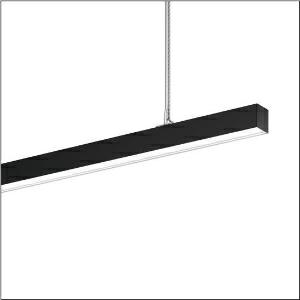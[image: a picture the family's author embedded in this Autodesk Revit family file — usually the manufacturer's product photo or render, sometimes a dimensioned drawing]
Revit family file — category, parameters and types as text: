
# Revit family: silica_r__21_51mx30db35bb_2e66
name_source: partatom
category: Lighting Fixtures
units: mm (PartAtom-declared; Revit-internal decimal feet)

## family parameters
Cut with Voids When Loaded = No
Host = Face
Light Source = No
Part Type = Normal
Room Calculation Point = No
Round Connector Dimension = Use Diameter
Shared = No

## types (1)
- --- (1 x LED, 5260 lm, 34.1 W, 3000K)
    Apparent Load = 34 VA
    CIE Flux Codes = 47 79 96 57 100
    Color Rendering = 80
    Color Temperature = 3000K
    Default Elevation = 1800 mm
    Description = Silica® 21, office luminaire, primary optical cover: cover, of PMMA, opal, light emission: direct/indirect distribution, primary light characteristic: symmetric, installation type: suspended mounting, LED, rated luminous flux: 5.260lm, luminous efficacy: 154lm/W, light colour: 830, colour temperature: 3000K, with terminal, 3+2-pole, max. 2.5mm², mains connection: 220..240V, AC, 50/60Hz, rated input power: 34.1W, luminaire housing, of aluminium, jet black (RAL 9005), length: 1.504mm, width: 53mm, height: 53mm, protection rating (complete): IP20, insulation class (complete): insulation class I (protective earthing), certification: CE, permissible operating ambient temperature: 0..+35°C, standard: EN 50419, packaging unit: 1 piece
    Height = 53 mm
    Lamp = 1 x LED
    Lamp Light Flux = 5260 lm
    Lamp Power = 34.1 W
    Lamp count = 1
    Length = 1504 mm
    Luminous efficacy = 154 lm/W
    Manufacturer = Siteco
    ModVariant = No
    Model = 51MX30DB35BB
    Mounting Place = Ceiling
    Mounting Type = Pendant
    Number of Poles = 1
    OnlyDefault = Yes
    Power Factor = 1
    Product Name = Silica® 21
    Product group = office luminaire | ceiling pendant
    ProductGroupID = 902
    Protection Class = Protection class I
    Protection Degree = IP 20
    RLX_Detail_Level = 1
    RLX_Emergency_Light_Flux = 0 lm
    RLX_Emergency_Type = 0
    RLX_Emergency_Type_DB = No
    RlxData = <blob elided: 26009 chars, md5=28c731c8>
    Socket = socket
    Standby Power = 0 W
    System Light Flux = 5260 lm
    System Power = 34 W
    Type Comments = factory setting: luminous flux: 100 % | dim-lin: 254 | 233 mA
    Type Image = l_1297744.jpg
    URL = http://relux.com
    VarID = @adj_047017
    Voltage = 0 V
    Weight = 0.00 kg
    Width = 53 mm

## geometry (parser evidence)
native form markers: Blend x4, Sweep x13
no freeform markers — native parametric forms only
